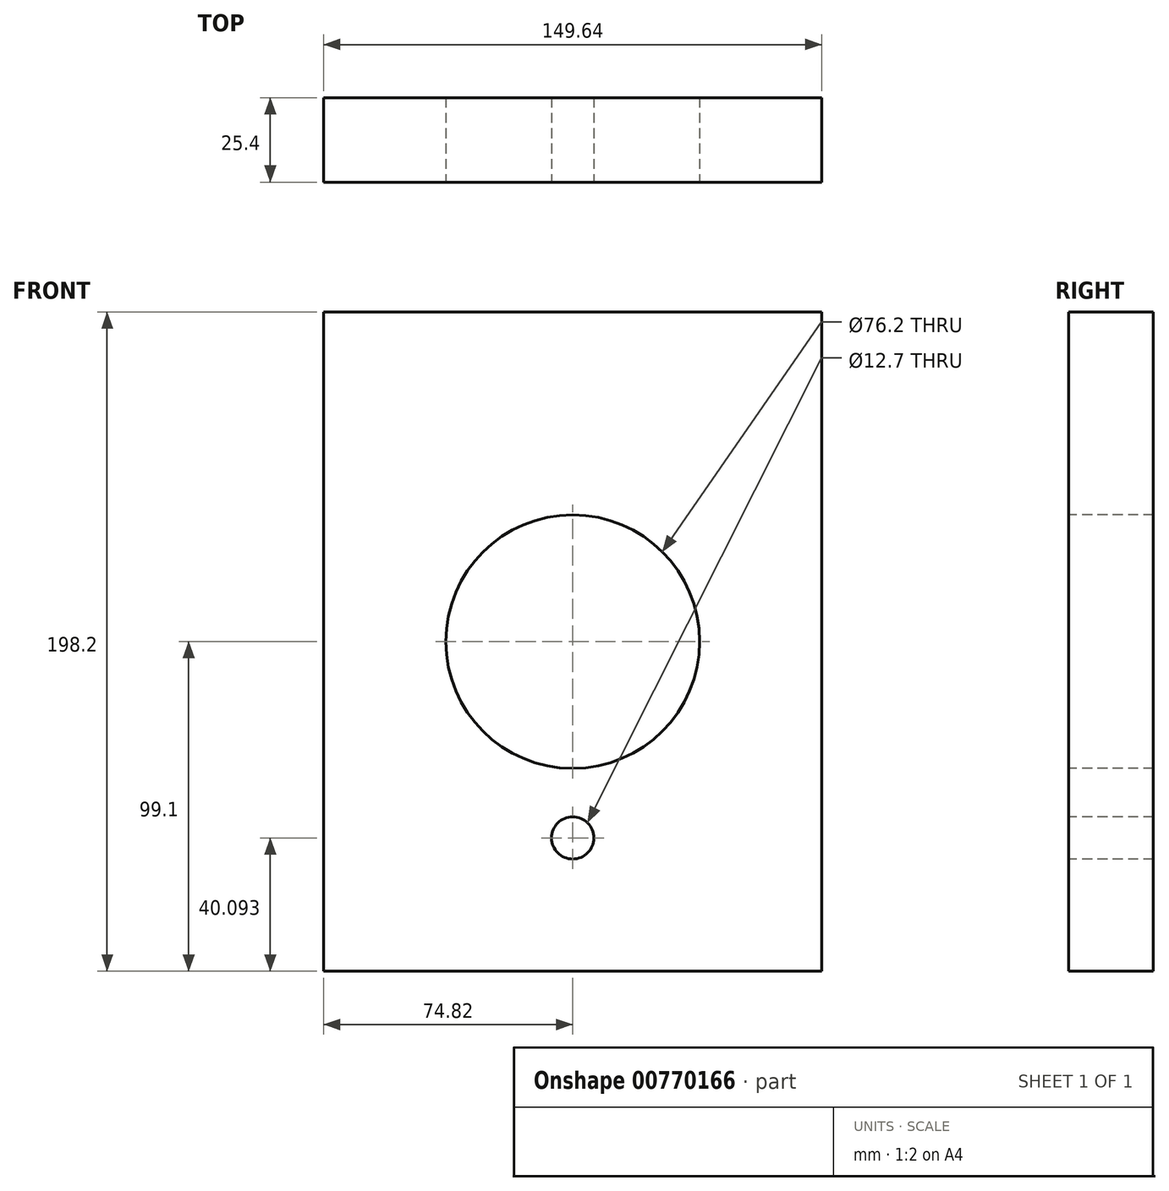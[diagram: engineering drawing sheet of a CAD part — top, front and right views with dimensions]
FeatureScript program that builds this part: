
annotation { "Feature Type Name" : "Feature", "Feature Type Description" : "" }
export const myFeature = defineFeature(function(context is Context, id is Id, definition is map)
    precondition{}
    {
        {
            var Q0;
            Q0=qCreatedBy(makeId("Front.planeOp"),FACE);
            var sketch = newSketch(context, id + "F0", { "sketchPlane" : qUnion([Q0])});
            skLineSegment(sketch, "E0.bottom", {"start": v(-74.82, 99.1) * mm, "end": v(74.82, 99.1) * mm});
            skLineSegment(sketch, "E0.top", {"start": v(-74.82, -99.1) * mm, "end": v(74.82, -99.1) * mm});
            skLineSegment(sketch, "E0.left", {"start": v(-74.82, 99.1) * mm, "end": v(-74.82, -99.1) * mm});
            skLineSegment(sketch, "E0.right", {"start": v(74.82, 99.1) * mm, "end": v(74.82, -99.1) * mm});
            skPoint(sketch, "E0.middle", {"position": v(0, 0) * mm});
            skSolve(sketch);
        }
        {
            var Q0;
            Q0 = qSketchRegion(id + "F0", true);
            extrude(context, id + "F1", {"entities" : qUnion([Q0]), "depth" : 25.4 * mm, "offsetDistance" : 25.4 * mm});
        }
        {
            var Q0;
            Q0=makeQuery(id+"F1.opExtrude","CAP_FACE",FACE,{"disambiguationData":[OSD([sQuery(id+"F0.wireOp",EDGE,"E0.bottom"),sQuery(id+"F0.wireOp",EDGE,"E0.top"),sQuery(id+"F0.wireOp",EDGE,"E0.left"),sQuery(id+"F0.wireOp",EDGE,"E0.right")])],"isStart":false});
            var sketch = newSketch(context, id + "F2", { "sketchPlane" : qUnion([Q0])});
            skCircle(sketch, "E1", {"center": v(0, 0) * mm, "radius": 37.92 * mm});
            skSolve(sketch);
        }
        {
            var Q0;
            Q0=sQuery(id+"F2.wireOp",VERTEX,"E1.center");
            var Q1;
            Q1=makeQuery(id+"F1.opExtrude","SWEPT_BODY",BODY,{"disambiguationData":[OSD([sQuery(id+"F0.wireOp",EDGE,"E0.bottom"),sQuery(id+"F0.wireOp",EDGE,"E0.top"),sQuery(id+"F0.wireOp",EDGE,"E0.left"),sQuery(id+"F0.wireOp",EDGE,"E0.right")])]});
            hole(context, id + "F3", {"style" : HoleStyle.SIMPLE, "endStyle" : HoleEndStyle.THROUGH, "holeDiameter" : 76.2 * mm, "majorDiameter" : 6.35 * mm, "isTappedThrough" : true, "tappedDepth" : 12.7 * mm, "tapClearance" : 3, "locations" : qUnion([Q0]), "scope" : qUnion([Q1])});
        }
        {
            var Q0;
            Q0=makeQuery(id+"F1.opExtrude","CAP_FACE",FACE,{"disambiguationData":[OSD([sQuery(id+"F0.wireOp",EDGE,"E0.bottom"),sQuery(id+"F0.wireOp",EDGE,"E0.top"),sQuery(id+"F0.wireOp",EDGE,"E0.left"),sQuery(id+"F0.wireOp",EDGE,"E0.right")])],"isStart":false});
            var sketch = newSketch(context, id + "F4", { "sketchPlane" : qUnion([Q0])});
            skCircle(sketch, "E2", {"center": v(0, -59) * mm, "radius": 12.77 * mm});
            skSolve(sketch);
        }
        {
            var Q0;
            Q0=sQuery(id+"F4.wireOp",VERTEX,"E2.center");
            var Q1;
            Q1=makeQuery(id+"F1.opExtrude","SWEPT_BODY",BODY,{"disambiguationData":[OSD([sQuery(id+"F0.wireOp",EDGE,"E0.bottom"),sQuery(id+"F0.wireOp",EDGE,"E0.top"),sQuery(id+"F0.wireOp",EDGE,"E0.left"),sQuery(id+"F0.wireOp",EDGE,"E0.right")])]});
            hole(context, id + "F5", {"style" : HoleStyle.SIMPLE, "endStyle" : HoleEndStyle.THROUGH, "holeDiameter" : 12.7 * mm, "majorDiameter" : 6.35 * mm, "isTappedThrough" : true, "tappedDepth" : 12.7 * mm, "tapClearance" : 3, "locations" : qUnion([Q0]), "scope" : qUnion([Q1])});
        }
    });
